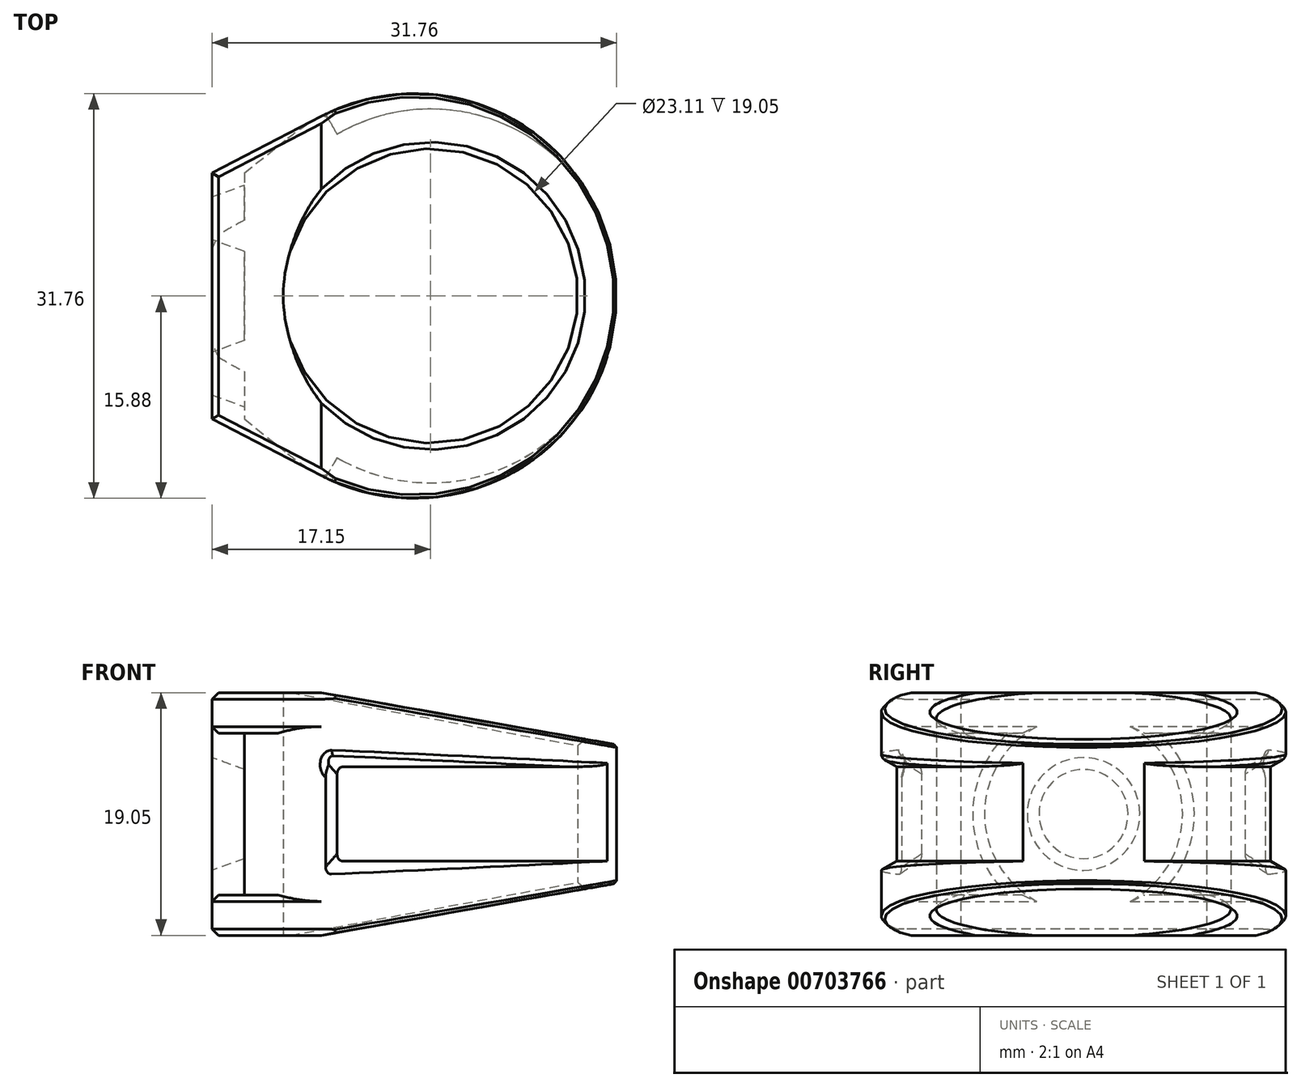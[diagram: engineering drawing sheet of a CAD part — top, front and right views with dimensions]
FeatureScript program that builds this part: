
annotation { "Feature Type Name" : "Feature", "Feature Type Description" : "" }
export const myFeature = defineFeature(function(context is Context, id is Id, definition is map)
    precondition{}
    {
        {
            var Q0;
            Q0=qCreatedBy(makeId("Top.planeOp"),FACE);
            var sketch = newSketch(context, id + "F0", { "sketchPlane" : qUnion([Q0])});
            skCircle(sketch, "E0", {"center": v(0, 0) * mm, "radius": 11.56 * mm});
            skCircle(sketch, "E1", {"center": v(-1.27, 0) * mm, "radius": 15.88 * mm});
            skSolve(sketch);
        }
        {
            var Q0;
            Q0 = qSketchRegion(id + "F0", true);
            extrude(context, id + "F1", {"entities" : qUnion([Q0]), "depth" : 19.05 * mm, "offsetDistance" : 25.4 * mm});
        }
        {
            var Q0;
            Q0=makeQuery(id+"F1.opExtrude","CAP_FACE",FACE,{"disambiguationData":[OSD([sQuery(id+"F0.wireOp",EDGE,"E0"),sQuery(id+"F0.wireOp",EDGE,"E1")])],"isStart":false});
            var sketch = newSketch(context, id + "F2", { "sketchPlane" : qUnion([Q0])});
            skLineSegment(sketch, "E2", {"start": v(-17.14, 7.62) * mm, "end": v(-17.14, -7.62) * mm});
            skPoint(sketch, "E3", {"position": v(-17.14, 0) * mm});
            skLineSegment(sketch, "E4", {"start": v(-17.15, 7.62) * mm, "end": v(-11.2, 12.39) * mm});
            skLineSegment(sketch, "E5", {"start": v(-17.15, -7.62) * mm, "end": v(-11.2, -12.39) * mm});
            skArc(sketch, "E6", {"start": v(-11.2, 12.39) * mm, "mid": v(-16.7, 0) * mm, "end": v(-11.2, -12.39) * mm});
            skSolve(sketch);
        }
        {
            var Q0;
            Q0 = qSketchRegion(id + "F2", true);
            var Q1;
            Q1=makeQuery(id+"F1.opExtrude","CAP_FACE",FACE,{"disambiguationData":[OSD([sQuery(id+"F0.wireOp",EDGE,"E0"),sQuery(id+"F0.wireOp",EDGE,"E1")])],"isStart":true});
            extrude(context, id + "F3", {"entities" : qUnion([Q0]), "operationType" : NewBodyOperationType.ADD, "endBound" : BoundingType.UP_TO_SURFACE, "oppositeDirection" : true, "depth" : 25.4 * mm, "endBoundEntityFace" : qUnion([Q1]), "offsetDistance" : 25.4 * mm});
        }
        {
            var Q0;
            Q0=makeQuery(id+"F3.opExtrude","SWEPT_FACE",FACE,{"disambiguationData":[OSD([sQuery(id+"F2.wireOp",EDGE,"E2")])]});
            var sketch = newSketch(context, id + "F4", { "sketchPlane" : qUnion([Q0])});
            skLineSegment(sketch, "E7.bottom", {"start": v(-7.62, 19.05) * mm, "end": v(7.62, 19.05) * mm});
            skLineSegment(sketch, "E7.top", {"start": v(-7.62, 0) * mm, "end": v(7.62, 0) * mm});
            skLineSegment(sketch, "E7.left", {"start": v(-7.62, 19.05) * mm, "end": v(-7.62, 0) * mm});
            skLineSegment(sketch, "E7.right", {"start": v(7.62, 19.05) * mm, "end": v(7.62, 0) * mm});
            skSolve(sketch);
        }
        {
            var Q0;
            Q0 = qSketchRegion(id + "F4", true);
            extrude(context, id + "F5", {"entities" : qUnion([Q0]), "operationType" : NewBodyOperationType.REMOVE, "oppositeDirection" : true, "depth" : 2.54 * mm, "offsetDistance" : 25.4 * mm, "hasDraft" : true, "draftAngle" : 45 * degree});
        }
        {
            var Q0;
            Q0=makeQuery(id+"F5.boolean.opBoolean","COPY",FACE,{"derivedFrom":makeQuery(id+"F5.opExtrude","CAP_FACE",FACE,{"disambiguationData":[OSD([sQuery(id+"F4.wireOp",EDGE,"E7.bottom"),sQuery(id+"F4.wireOp",EDGE,"E7.top"),sQuery(id+"F4.wireOp",EDGE,"E7.left"),sQuery(id+"F4.wireOp",EDGE,"E7.right")])],"isStart":false})});
            var sketch = newSketch(context, id + "F6", { "sketchPlane" : qUnion([Q0])});
            skCircle(sketch, "E8", {"center": v(0, 9.53) * mm, "radius": 8.7 * mm});
            skCircle(sketch, "E9", {"center": v(0, 9.53) * mm, "radius": 3.5 * mm});
            skSolve(sketch);
        }
        {
            var Q0;
            Q0 = qSketchRegion(id + "F6", true);
            extrude(context, id + "F7", {"entities" : qUnion([Q0]), "operationType" : NewBodyOperationType.ADD, "depth" : 2.54 * mm, "offsetDistance" : 25.4 * mm, "hasDraft" : true, "draftAngle" : 20 * degree, "draftPullDirection" : true});
        }
        {
            var Q0;
            {var subQ1=sQuery(id+"F2.wireOp",EDGE,"E4");Q0=makeQuery(id+"F7.boolean.opBoolean","SPLIT",FACE,{"disambiguationData":[TD([makeQuery(id+"F3.opExtrude","SWEPT_FACE",FACE,{"disambiguationData":[OSD([subQ1])]})])],"derivedFrom":makeQuery(id+"F5.boolean.opBoolean","COPY",FACE,{"derivedFrom":makeQuery(id+"F5.opExtrude","CAP_FACE",FACE,{"disambiguationData":[OSD([sQuery(id+"F4.wireOp",EDGE,"E7.bottom"),sQuery(id+"F4.wireOp",EDGE,"E7.top"),sQuery(id+"F4.wireOp",EDGE,"E7.left"),sQuery(id+"F4.wireOp",EDGE,"E7.right")])],"isStart":false})})});}
            var sketch = newSketch(context, id + "F8", { "sketchPlane" : qUnion([Q0])});
            skLineSegment(sketch, "E10.bottom", {"start": v(-9.66, 19.05) * mm, "end": v(9.66, 19.05) * mm});
            skLineSegment(sketch, "E10.top", {"start": v(-9.66, 15.87) * mm, "end": v(9.66, 15.87) * mm});
            skLineSegment(sketch, "E10.left", {"start": v(-9.66, 19.05) * mm, "end": v(-9.66, 15.88) * mm});
            skLineSegment(sketch, "E10.right", {"start": v(9.66, 19.05) * mm, "end": v(9.66, 15.87) * mm});
            skLineSegment(sketch, "E11.bottom", {"start": v(-9.66, 0) * mm, "end": v(9.66, 0) * mm});
            skLineSegment(sketch, "E11.top", {"start": v(-9.66, 3.17) * mm, "end": v(9.66, 3.17) * mm});
            skLineSegment(sketch, "E11.left", {"start": v(-9.66, 0) * mm, "end": v(-9.66, 3.17) * mm});
            skLineSegment(sketch, "E11.right", {"start": v(9.66, 0) * mm, "end": v(9.66, 3.17) * mm});
            skSolve(sketch);
        }
        {
            var Q0;
            Q0 = qSketchRegion(id + "F8", true);
            extrude(context, id + "F9", {"entities" : qUnion([Q0]), "operationType" : NewBodyOperationType.ADD, "depth" : 2.54 * mm, "offsetDistance" : 25.4 * mm});
        }
        {
            var Q0;
            Q0=makeQuery(id+"F9.boolean.opBoolean","MERGE",FACE,{"derivedFrom":[makeQuery(id+"F3.boolean.opBoolean","MERGE",FACE,{"derivedFrom":[makeQuery(id+"F1.opExtrude","CAP_FACE",FACE,{"disambiguationData":[OSD([sQuery(id+"F0.wireOp",EDGE,"E0"),sQuery(id+"F0.wireOp",EDGE,"E1")])],"isStart":false}),makeQuery(id+"F3.opExtrude","CAP_FACE",FACE,{"disambiguationData":[OSD([sQuery(id+"F2.wireOp",EDGE,"E2"),sQuery(id+"F2.wireOp",EDGE,"E4"),sQuery(id+"F2.wireOp",EDGE,"E5"),sQuery(id+"F2.wireOp",EDGE,"E6")])],"isStart":true})]}),makeQuery(id+"F9.opExtrude","SWEPT_FACE",FACE,{"disambiguationData":[OSD([sQuery(id+"F8.wireOp",EDGE,"E10.bottom")])]})]});
            var sketch = newSketch(context, id + "F10", { "sketchPlane" : qUnion([Q0])});
            skLineSegment(sketch, "E12", {"start": v(-8.57, 14.1) * mm, "end": v(-17.14, 9.66) * mm});
            skLineSegment(sketch, "E13", {"start": v(-8.57, -14.1) * mm, "end": v(-17.14, -9.66) * mm});
            skLineSegment(sketch, "E14", {"start": v(-17.14, 9.66) * mm, "end": v(-17.14, -9.66) * mm});
            skArc(sketch, "E15", {"start": v(-8.57, 14.1) * mm, "mid": v(-13.8, 0) * mm, "end": v(-8.57, -14.1) * mm});
            skSolve(sketch);
        }
        {
            var Q0;
            Q0 = qSketchRegion(id + "F10", true);
            extrude(context, id + "F11", {"entities" : qUnion([Q0]), "operationType" : NewBodyOperationType.ADD, "oppositeDirection" : true, "depth" : 3.17 * mm, "offsetDistance" : 25.4 * mm});
        }
        {
            var Q0;
            {var subQ0=sQuery(id+"F0.wireOp",EDGE,"E1");var subQ1=sQuery(id+"F0.wireOp",EDGE,"E0");Q0=makeQuery(id+"F9.boolean.opBoolean","MERGE",FACE,{"derivedFrom":[makeQuery(id+"F3.boolean.opBoolean","MERGE",FACE,{"derivedFrom":[makeQuery(id+"F1.opExtrude","CAP_FACE",FACE,{"disambiguationData":[OSD([subQ1,subQ0])],"isStart":true}),makeQuery(id+"F3.opExtrude","CAP_FACE",FACE,{"disambiguationData":[OSD([subQ1,subQ0])],"isStart":false})]}),makeQuery(id+"F9.opExtrude","SWEPT_FACE",FACE,{"disambiguationData":[OSD([sQuery(id+"F8.wireOp",EDGE,"E11.bottom")])]})]});}
            var sketch = newSketch(context, id + "F12", { "sketchPlane" : qUnion([Q0])});
            skLineSegment(sketch, "E16", {"start": v(-17.14, 9.66) * mm, "end": v(-8.57, 14.1) * mm});
            skLineSegment(sketch, "E17", {"start": v(-17.14, -9.66) * mm, "end": v(-8.57, -14.1) * mm});
            skLineSegment(sketch, "E18", {"start": v(-17.14, -9.66) * mm, "end": v(-17.14, 9.66) * mm});
            skArc(sketch, "E19", {"start": v(-8.57, 14.1) * mm, "mid": v(-13.8, 0) * mm, "end": v(-8.57, -14.1) * mm});
            skSolve(sketch);
        }
        {
            var Q0;
            Q0 = qSketchRegion(id + "F12", true);
            extrude(context, id + "F13", {"entities" : qUnion([Q0]), "operationType" : NewBodyOperationType.ADD, "oppositeDirection" : true, "depth" : 3.17 * mm, "offsetDistance" : 25.4 * mm});
        }
        {
            var Q0;
            Q0=qCreatedBy(makeId("Front.planeOp"),FACE);
            cPlane(context, id + "F14", {"entities" : qUnion([Q0]), "cplaneType" : CPlaneType.OFFSET, "offset" : 17.78 * mm, "width" : 152.4 * mm, "height" : 152.4 * mm});
        }
        {
            var Q0;
            Q0=qCreatedBy(id+"F14.planeOp",FACE);
            var sketch = newSketch(context, id + "F15", { "sketchPlane" : qUnion([Q0])});
            skLineSegment(sketch, "E20", {"start": v(-8.57, 19.05) * mm, "end": v(17.78, 14.4) * mm});
            skLineSegment(sketch, "E21", {"start": v(-8.57, 0) * mm, "end": v(17.78, 4.65) * mm});
            skLineSegment(sketch, "E22", {"start": v(-8.57, 19.05) * mm, "end": v(17.78, 19.05) * mm});
            skLineSegment(sketch, "E23", {"start": v(-8.57, 0) * mm, "end": v(17.78, 0) * mm});
            skLineSegment(sketch, "E24", {"start": v(17.78, 0) * mm, "end": v(17.78, 4.65) * mm});
            skLineSegment(sketch, "E25", {"start": v(17.78, 14.4) * mm, "end": v(17.78, 19.05) * mm});
            skSolve(sketch);
        }
        {
            var Q0;
            Q0 = qSketchRegion(id + "F15", true);
            extrude(context, id + "F16", {"entities" : qUnion([Q0]), "operationType" : NewBodyOperationType.REMOVE, "endBound" : BoundingType.THROUGH_ALL, "oppositeDirection" : true, "depth" : 25.4 * mm, "offsetDistance" : 25.4 * mm});
        }
        {
            var Q0;
            Q0=qCreatedBy(makeId("Right.planeOp"),FACE);
            var sketch = newSketch(context, id + "F17", { "sketchPlane" : qUnion([Q0])});
            skLineSegment(sketch, "E26", {"start": v(-16.51, 4.76) * mm, "end": v(-16.51, 14.29) * mm});
            skLineSegment(sketch, "E27", {"start": v(-16.51, 14.29) * mm, "end": v(-14.67, 13.22) * mm});
            skLineSegment(sketch, "E28", {"start": v(-14.67, 5.83) * mm, "end": v(-16.51, 4.76) * mm});
            skLineSegment(sketch, "E29", {"start": v(-14.67, 5.83) * mm, "end": v(-14.67, 13.22) * mm});
            skPoint(sketch, "E30", {"position": v(-16.51, 9.52) * mm});
            skPoint(sketch, "E31", {"position": v(-14.67, 9.52) * mm});
            skLineSegment(sketch, "E32", {"start": v(0, 0) * mm, "end": v(0, 21.81) * mm, "construction": true});
            skSolve(sketch);
        }
        {
            var Q0;
            Q0 = qSketchRegion(id + "F17", true);
            var Q1;
            Q1=sQuery(id+"F17.wireOp",EDGE,"E32");
            revolve(context, id + "F18", {"operationType" : NewBodyOperationType.REMOVE, "surfaceOperationType" : NewSurfaceOperationType.NEW, "entities" : qUnion([Q0]), "axis" : qUnion([Q1]), "revolveType" : RevolveType.TWO_DIRECTIONS, "angle" : 210 * degree, "angleBack" : 330 * degree});
        }
        {
            var Q0;
            Q0=makeQuery(id+"F16.boolean.opBoolean","INTERSECT",EDGE,{"derivedFrom":[makeQuery(id+"F1.opExtrude","SWEPT_FACE",FACE,{"disambiguationData":[OSD([sQuery(id+"F0.wireOp",EDGE,"E0")])]}),makeQuery(id+"F16.opExtrude","SWEPT_FACE",FACE,{"disambiguationData":[OSD([sQuery(id+"F15.wireOp",EDGE,"E20")])]})]});
            var Q1;
            Q1=makeQuery(id+"F16.boolean.opBoolean","INTERSECT",EDGE,{"derivedFrom":[makeQuery(id+"F1.opExtrude","SWEPT_FACE",FACE,{"disambiguationData":[OSD([sQuery(id+"F0.wireOp",EDGE,"E0")])]}),makeQuery(id+"F16.opExtrude","SWEPT_FACE",FACE,{"disambiguationData":[OSD([sQuery(id+"F15.wireOp",EDGE,"E21")])]})]});
            chamfer(context, id + "F19", {"entities" : qUnion([Q0, Q1]), "width" : 0.5 * mm, "tangentPropagation" : true});
        }
        {
            var Q0;
            Q0=makeQuery(id+"F9.opExtrude","CAP_EDGE",EDGE,{"disambiguationData":[OSD([sQuery(id+"F8.wireOp",EDGE,"E10.bottom")])],"isStart":false});
            var Q1;
            Q1=makeQuery(id+"F9.opExtrude","CAP_EDGE",EDGE,{"disambiguationData":[OSD([sQuery(id+"F8.wireOp",EDGE,"E11.bottom")])],"isStart":false});
            var Q2;
            {var subQ1=sQuery(id+"F8.wireOp",EDGE,"E11.left");var subQ2=sQuery(id+"F8.wireOp",EDGE,"E11.top");Q2=makeQuery(id+"F9.boolean.opBoolean","SPLIT",EDGE,{"disambiguationData":[TD([makeQuery(id+"F9.opExtrude","SWEPT_FACE",FACE,{"disambiguationData":[OSD([subQ1])]})])],"derivedFrom":makeQuery(id+"F9.opExtrude","CAP_EDGE",EDGE,{"disambiguationData":[OSD([subQ2])],"isStart":false})});}
            var Q3;
            {var subQ1=sQuery(id+"F8.wireOp",EDGE,"E11.right");var subQ2=sQuery(id+"F8.wireOp",EDGE,"E11.top");Q3=makeQuery(id+"F9.boolean.opBoolean","SPLIT",EDGE,{"disambiguationData":[TD([makeQuery(id+"F9.opExtrude","SWEPT_FACE",FACE,{"disambiguationData":[OSD([subQ1])]})])],"derivedFrom":makeQuery(id+"F9.opExtrude","CAP_EDGE",EDGE,{"disambiguationData":[OSD([subQ2])],"isStart":false})});}
            var Q4;
            {var subQ0=sQuery(id+"F8.wireOp",EDGE,"E10.right");var subQ1=sQuery(id+"F8.wireOp",EDGE,"E10.top");Q4=makeQuery(id+"F9.boolean.opBoolean","SPLIT",EDGE,{"disambiguationData":[TD([makeQuery(id+"F9.opExtrude","SWEPT_FACE",FACE,{"disambiguationData":[OSD([subQ0])]})])],"derivedFrom":makeQuery(id+"F9.opExtrude","CAP_EDGE",EDGE,{"disambiguationData":[OSD([subQ1])],"isStart":false})});}
            var Q5;
            {var subQ0=sQuery(id+"F8.wireOp",EDGE,"E10.left");var subQ1=sQuery(id+"F8.wireOp",EDGE,"E10.top");Q5=makeQuery(id+"F9.boolean.opBoolean","SPLIT",EDGE,{"disambiguationData":[TD([makeQuery(id+"F9.opExtrude","SWEPT_FACE",FACE,{"disambiguationData":[OSD([subQ0])]})])],"derivedFrom":makeQuery(id+"F9.opExtrude","CAP_EDGE",EDGE,{"disambiguationData":[OSD([subQ1])],"isStart":false})});}
            var Q6;
            Q6=makeQuery(id+"F11.opExtrude","CAP_EDGE",EDGE,{"disambiguationData":[OSD([sQuery(id+"F10.wireOp",EDGE,"E13")])],"isStart":true});
            var Q7;
            Q7=makeQuery(id+"F11.opExtrude","CAP_EDGE",EDGE,{"disambiguationData":[OSD([sQuery(id+"F10.wireOp",EDGE,"E13")])],"isStart":false});
            var Q8;
            Q8=makeQuery(id+"F13.opExtrude","CAP_EDGE",EDGE,{"disambiguationData":[OSD([sQuery(id+"F12.wireOp",EDGE,"E16")])],"isStart":false});
            var Q9;
            Q9=makeQuery(id+"F13.opExtrude","CAP_EDGE",EDGE,{"disambiguationData":[OSD([sQuery(id+"F12.wireOp",EDGE,"E16")])],"isStart":true});
            var Q10;
            Q10=makeQuery(id+"F13.opExtrude","CAP_EDGE",EDGE,{"disambiguationData":[OSD([sQuery(id+"F12.wireOp",EDGE,"E17")])],"isStart":false});
            var Q11;
            Q11=makeQuery(id+"F13.opExtrude","CAP_EDGE",EDGE,{"disambiguationData":[OSD([sQuery(id+"F12.wireOp",EDGE,"E17")])],"isStart":true});
            var Q12;
            Q12=makeQuery(id+"F11.opExtrude","CAP_EDGE",EDGE,{"disambiguationData":[OSD([sQuery(id+"F10.wireOp",EDGE,"E12")])],"isStart":false});
            var Q13;
            Q13=makeQuery(id+"F11.opExtrude","CAP_EDGE",EDGE,{"disambiguationData":[OSD([sQuery(id+"F10.wireOp",EDGE,"E12")])],"isStart":true});
            chamfer(context, id + "F20", {"entities" : qUnion([Q0, Q1, Q2, Q3, Q4, Q5, Q6, Q7, Q8, Q9, Q10, Q11, Q12, Q13]), "width" : 0.5 * mm, "tangentPropagation" : true});
        }
        {
            var Q0;
            Q0=makeQuery(id+"F16.boolean.opBoolean","INTERSECT",EDGE,{"derivedFrom":[makeQuery(id+"F1.opExtrude","SWEPT_FACE",FACE,{"disambiguationData":[OSD([sQuery(id+"F0.wireOp",EDGE,"E1")])]}),makeQuery(id+"F16.opExtrude","SWEPT_FACE",FACE,{"disambiguationData":[OSD([sQuery(id+"F15.wireOp",EDGE,"E20")])]})]});
            var Q1;
            Q1=makeQuery(id+"F16.boolean.opBoolean","INTERSECT",EDGE,{"derivedFrom":[makeQuery(id+"F1.opExtrude","SWEPT_FACE",FACE,{"disambiguationData":[OSD([sQuery(id+"F0.wireOp",EDGE,"E1")])]}),makeQuery(id+"F16.opExtrude","SWEPT_FACE",FACE,{"disambiguationData":[OSD([sQuery(id+"F15.wireOp",EDGE,"E21")])]})]});
            chamfer(context, id + "F21", {"entities" : qUnion([Q0, Q1]), "width" : 0.25 * mm, "tangentPropagation" : true});
        }
        {
            var Q0;
            Q0=makeQuery(id+"F18.boolean.opBoolean","COPY",EDGE,{"derivedFrom":makeQuery(id+"F18.opRevolve","CAP_EDGE",EDGE,{"disambiguationData":[OSD([sQuery(id+"F17.wireOp",EDGE,"E27")])],"isStart":true})});
            var Q1;
            Q1=makeQuery(id+"F18.boolean.opBoolean","COPY",EDGE,{"derivedFrom":makeQuery(id+"F18.opRevolve","CAP_EDGE",EDGE,{"disambiguationData":[OSD([sQuery(id+"F17.wireOp",EDGE,"E28")])],"isStart":true})});
            var Q2;
            Q2=makeQuery(id+"F18.boolean.opBoolean","INTERSECT",EDGE,{"disambiguationData":[OD(0.0)],"derivedFrom":[makeQuery(id+"F1.opExtrude","SWEPT_FACE",FACE,{"disambiguationData":[OSD([sQuery(id+"F0.wireOp",EDGE,"E1")])]}),makeQuery(id+"F18.opRevolve","SWEPT_FACE",FACE,{"disambiguationData":[OSD([sQuery(id+"F17.wireOp",EDGE,"E27")])]})]});
            var Q3;
            Q3=makeQuery(id+"F18.boolean.opBoolean","COPY",EDGE,{"derivedFrom":makeQuery(id+"F18.opRevolve","CAP_EDGE",EDGE,{"disambiguationData":[OSD([sQuery(id+"F17.wireOp",EDGE,"E28")])],"isStart":false})});
            var Q4;
            Q4=makeQuery(id+"F18.boolean.opBoolean","COPY",EDGE,{"derivedFrom":makeQuery(id+"F18.opRevolve","CAP_EDGE",EDGE,{"disambiguationData":[OSD([sQuery(id+"F17.wireOp",EDGE,"E27")])],"isStart":false})});
            var Q5;
            Q5=makeQuery(id+"F18.boolean.opBoolean","INTERSECT",EDGE,{"disambiguationData":[OD(1.0)],"derivedFrom":[makeQuery(id+"F1.opExtrude","SWEPT_FACE",FACE,{"disambiguationData":[OSD([sQuery(id+"F0.wireOp",EDGE,"E1")])]}),makeQuery(id+"F18.opRevolve","SWEPT_FACE",FACE,{"disambiguationData":[OSD([sQuery(id+"F17.wireOp",EDGE,"E27")])]})]});
            fillet(context, id + "F22", {"entities" : qUnion([Q0, Q1, Q2, Q3, Q4, Q5]), "radius" : 0.5 * mm, "tangentPropagation" : true, "allowEdgeOverflow" : false});
        }
    });
